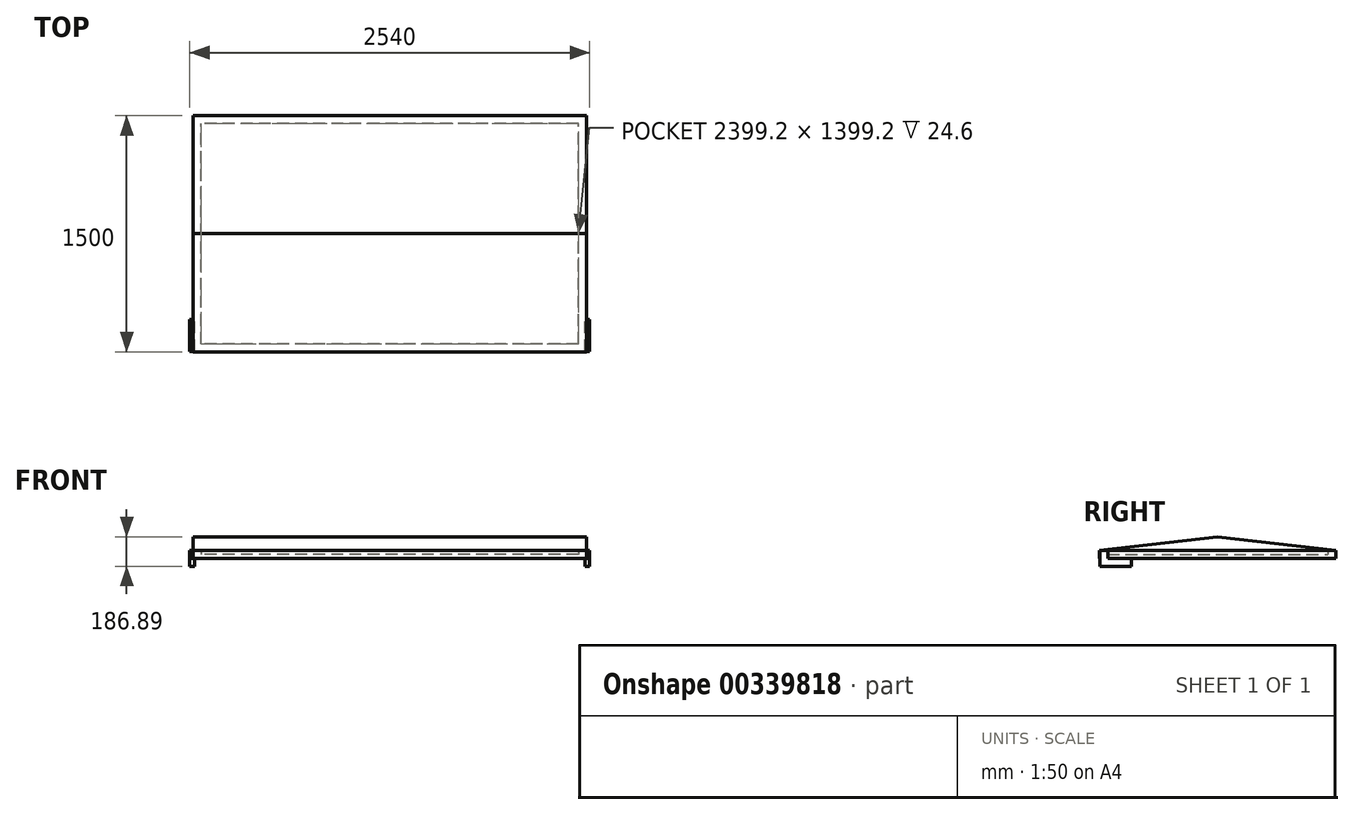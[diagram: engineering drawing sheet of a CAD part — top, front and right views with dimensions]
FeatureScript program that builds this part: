
annotation { "Feature Type Name" : "Feature", "Feature Type Description" : "" }
export const myFeature = defineFeature(function(context is Context, id is Id, definition is map)
    precondition{}
    {
        {
            var Q0;
            Q0=qCreatedBy(makeId("Top.planeOp"),FACE);
            var sketch = newSketch(context, id + "F0", { "sketchPlane" : qUnion([Q0])});
            skLineSegment(sketch, "E0.bottom", {"start": v(1250, 750) * mm, "end": v(-1250, 750) * mm});
            skLineSegment(sketch, "E0.top", {"start": v(1250, -750) * mm, "end": v(-1250, -750) * mm});
            skLineSegment(sketch, "E0.left", {"start": v(1250, 750) * mm, "end": v(1250, -750) * mm});
            skLineSegment(sketch, "E0.right", {"start": v(-1250, 750) * mm, "end": v(-1250, -750) * mm});
            skPoint(sketch, "E0.middle", {"position": v(0, 0) * mm});
            skLineSegment(sketch, "E1.bottom", {"start": v(1225, -725) * mm, "end": v(-1225, -725) * mm});
            skLineSegment(sketch, "E1.top", {"start": v(1225, 725) * mm, "end": v(-1225, 725) * mm});
            skLineSegment(sketch, "E1.left", {"start": v(1225, -725) * mm, "end": v(1225, 725) * mm});
            skLineSegment(sketch, "E1.right", {"start": v(-1225, -725) * mm, "end": v(-1225, 725) * mm});
            skSolve(sketch);
        }
        {
            var Q0;
            Q0=makeQuery(id+"F0.imprint","IMPRINT",FACE,{"disambiguationData":[TD([[makeQuery(id+"F0.imprint","IMPRINT",EDGE,{"derivedFrom":sQuery(id+"F0.wireOp",EDGE,"E1.bottom")}),-1.0]])]});
            extrude(context, id + "F1", {"entities" : qUnion([Q0]), "depth" : 50 * mm});
        }
        {
            var Q0;
            Q0=makeQuery(id+"F1.opExtrude","CAP_FACE",FACE,{"disambiguationData":[OSD([sQuery(id+"F0.wireOp",EDGE,"E1.bottom"),sQuery(id+"F0.wireOp",EDGE,"E1.top"),sQuery(id+"F0.wireOp",EDGE,"E1.left"),sQuery(id+"F0.wireOp",EDGE,"E1.right")])],"isStart":false});
            shell(context, id + "F2", {"entities" : qUnion([Q0]), "thickness" : 25.4 * mm});
        }
        {
            var Q0;
            Q0=makeQuery(id+"F0.imprint","IMPRINT",FACE,{"disambiguationData":[TD([[makeQuery(id+"F0.imprint","IMPRINT",EDGE,{"derivedFrom":sQuery(id+"F0.wireOp",EDGE,"E0.bottom")}),1.0]])]});
            extrude(context, id + "F3", {"entities" : qUnion([Q0]), "operationType" : NewBodyOperationType.ADD, "depth" : 50 * mm});
        }
        {
            var Q0;
            Q0=qCreatedBy(makeId("Right.planeOp"),FACE);
            var sketch = newSketch(context, id + "F4", { "sketchPlane" : qUnion([Q0])});
            skLineSegment(sketch, "E2", {"start": v(-750, 51.76) * mm, "end": v(750, 51.76) * mm});
            skLineSegment(sketch, "E3", {"start": v(750, 51.76) * mm, "end": v(0, 136.9) * mm});
            skLineSegment(sketch, "E4", {"start": v(0, 136.9) * mm, "end": v(-750, 51.76) * mm});
            skSolve(sketch);
        }
        {
            var Q0;
            Q0=makeQuery(id+"F4.imprint","IMPRINT",FACE,{"disambiguationData":[TD([[makeQuery(id+"F4.imprint","IMPRINT",EDGE,{"derivedFrom":sQuery(id+"F4.wireOp",EDGE,"E2")}),1.0]])]});
            extrude(context, id + "F5", {"entities" : qUnion([Q0]), "endBound" : BoundingType.SYMMETRIC, "depth" : 2500 * mm, "hasSecondDirection" : true, "secondDirectionOppositeDirection" : true, "secondDirectionDepth" : 25.4 * mm});
        }
        {
            var Q0;
            Q0=qCreatedBy(makeId("Right.planeOp"),FACE);
            var sketch = newSketch(context, id + "F6", { "sketchPlane" : qUnion([Q0])});
            skLineSegment(sketch, "E5.bottom", {"start": v(-746.02, 0) * mm, "end": v(-546.02, 0) * mm});
            skLineSegment(sketch, "E5.top", {"start": v(-746.02, -50) * mm, "end": v(-546.02, -50) * mm});
            skLineSegment(sketch, "E5.left", {"start": v(-746.02, 0) * mm, "end": v(-746.02, -50) * mm});
            skLineSegment(sketch, "E5.right", {"start": v(-546.02, 0) * mm, "end": v(-546.02, -50) * mm});
            skLineSegment(sketch, "E6.bottom", {"start": v(-747.5, 50) * mm, "end": v(-697.5, 50) * mm});
            skLineSegment(sketch, "E6.top", {"start": v(-747.5, 0) * mm, "end": v(-697.5, 0) * mm});
            skLineSegment(sketch, "E6.left", {"start": v(-747.5, 50) * mm, "end": v(-747.5, 0) * mm});
            skLineSegment(sketch, "E6.right", {"start": v(-697.5, 50) * mm, "end": v(-697.5, 0) * mm});
            skSolve(sketch);
        }
        {
            var Q0;
            Q0 = qSketchRegion(id + "F6", true);
            extrude(context, id + "F7", {"entities" : qUnion([Q0]), "operationType" : NewBodyOperationType.ADD, "oppositeDirection" : true, "depth" : 1270 * mm, "hasSecondDirection" : true, "secondDirectionOppositeDirection" : true, "secondDirectionDepth" : 1240 * mm});
        }
        {
            var Q0;
            Q0 = qSketchRegion(id + "F6", true);
            extrude(context, id + "F8", {"entities" : qUnion([Q0]), "operationType" : NewBodyOperationType.ADD, "depth" : 1270 * mm, "hasSecondDirection" : true, "secondDirectionOppositeDirection" : false, "secondDirectionDepth" : 1240 * mm});
        }
    });
